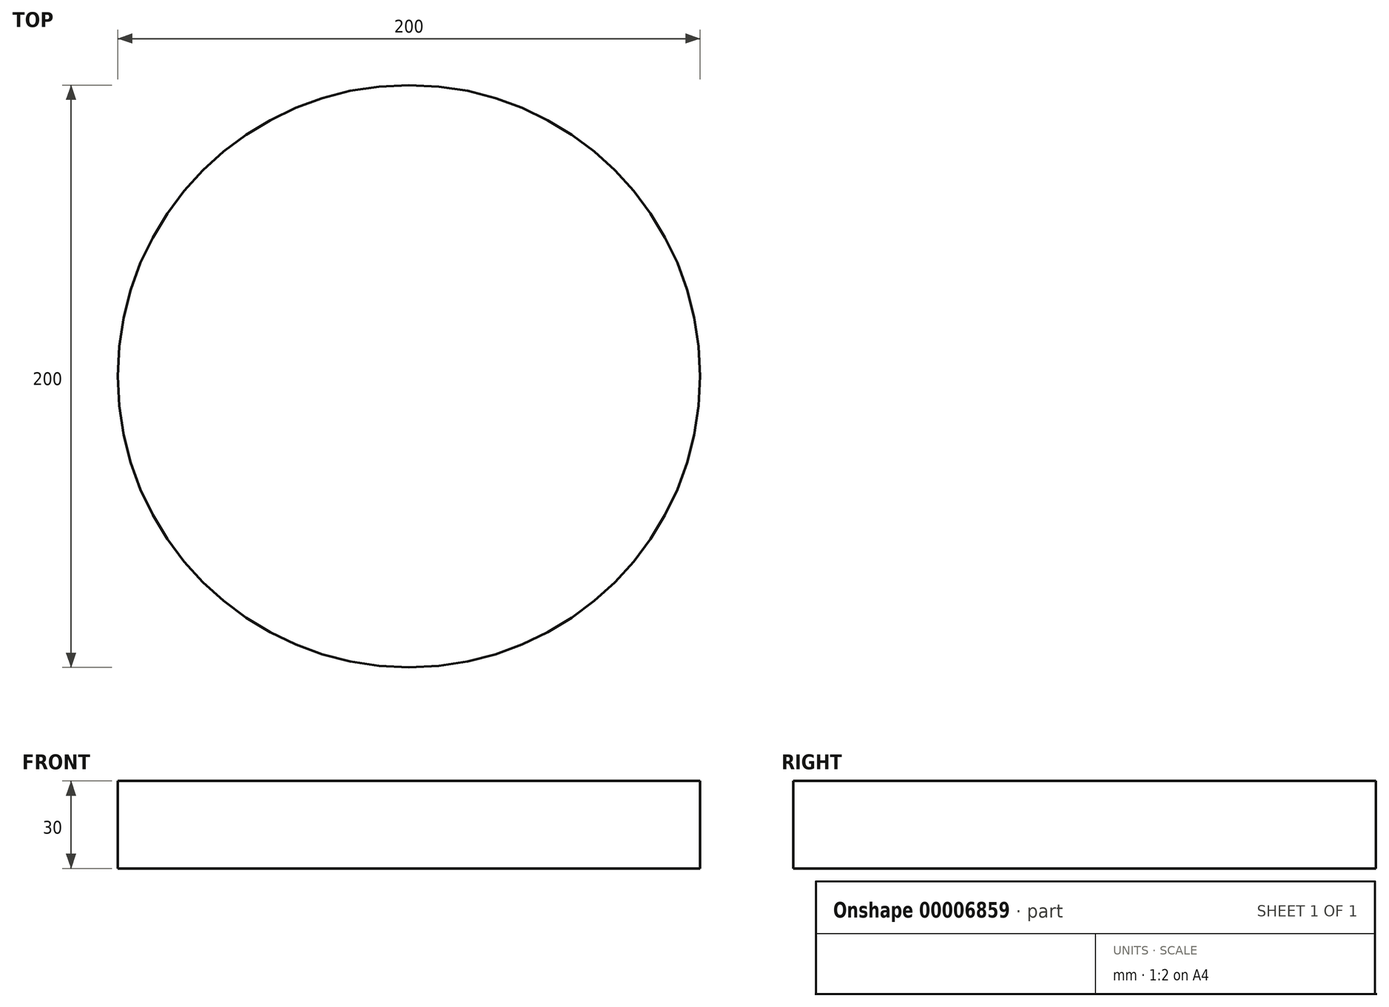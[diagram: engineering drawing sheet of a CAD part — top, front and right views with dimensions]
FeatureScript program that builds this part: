
annotation { "Feature Type Name" : "Feature", "Feature Type Description" : "" }
export const myFeature = defineFeature(function(context is Context, id is Id, definition is map)
    precondition{}
    {
        {
            var Q0;
            Q0=qCreatedBy(makeId("Top.planeOp"),FACE);
            var sketch = newSketch(context, id + "F0", { "sketchPlane" : qUnion([Q0])});
            skCircle(sketch, "E0", {"center": v(0, 0) * mm, "radius": 100 * mm});
            skSolve(sketch);
        }
        {
            var Q0;
            Q0 = qSketchRegion(id + "F0", true);
            extrude(context, id + "F1", {"entities" : qUnion([Q0]), "depth" : 30 * mm});
        }
    });
